# Revit family: OPUS-B
name_source: partatom
category: Mechanical Equipment
revit_build: Autodesk Revit 2015 (Build: 20140606_1530(x64)
units: mm (PartAtom-declared; Revit-internal decimal feet)

## types (6) — shared parameters
Catalogue Pages = http://www.nuaire.info
Depth = 160 mm  [stored 0.524934 ft]
Electrical Phase = 1
Fax Number = +44(0)2920-858-222
Height = 320 mm  [stored 1.04987 ft]
I&M Manual = http://www.nuaire.info
IFCExportAs = IfcFanType
Manufacturer = Nuaire
Manufacturer Name = Nuaire
Maximum Ambient Temperature = 40 °C
OmniClass Number = 23-33 31 19 13
OmniClass Title = Centrifugal Fans
Postcode = CF83 1NA
Revit Family Last Revised = 30/10/18
Spigot Diameter = 125 mm  [stored 0.410105 ft]
Spigot Radius = 63 mm
Telephone Number = +44(0)2920-858-200
URL = http://www.nuaire.co.uk
VAT Registration Number = 877308
Voltage = 230 V
Warranty Period = 3 Years
Weatherproof or Internal Only = Internal
Weight = 6.00 kg
Width = 335 mm  [stored 1.09908 ft]

## per-type parameters (varying)
| type | Apparent Load | Classification.Uniclass.Pr.Description | Classification.Uniclass.Pr.Number | Description | Full Load Current | Model | Nuaire Model Code | Number of Connection Poles | PIR | Starting Current | Unit Description |
| OPUS150-BP | 179 VA | Centrifugal fans | Pr_65_67_29_12 | Surface Mounted Fan Unit with Integral PIR | 1 A | OPUS150-BP | OPUS150-BP | 2 | Yes | 1 A | Surface Mounted Fan Unit with Integral PIR |
| OPUS100-BP | 90 VA | Centrifugal fans | Pr_65_67_29_12 | Surface Mounted Fan Unit with Integral PIR | 0 A | OPUS100-BP | OPUS100-BP | 1 | Yes | 0 A | Surface Mounted Fan Unit with Integral PIR |
| OPUS100-B | 90 VA | Centrifugal fans | Pr_65_67_29_12 | Surface Mounted Fan Unit | 0 A | OPUS100-B | OPUS100-B | 1 | No | 0 A | Surface Mounted Fan Unit |
| OPUS150-B | 179 VA | Centrifugal fans | Pr_65_67_29_12 | Surface Mounted Fan Unit | 1 A | OPUS150-BP | OPUS150-BP | 1 | No | 1 A | Surface Mounted Fan Unit |
| OPUS100-2B | 90 VA | Twin centrifugal fans | Pr_65_67_29_89 | Surface Mounted Twin Fan Unit | 0 A | OPUS100-2B | OPUS100-2B | 1 | No | 0 A | Surface Mounted Twin Fan Unit |
| OPUS100-2BP | 90 VA | Twin centrifugal fans | Pr_65_67_29_89 | Surface Mounted Twin Fan Unit with integral PIR | 0 A | OPUS100-2B | OPUS100-2B | 1 | Yes | 0 A | Surface Mounted Twin Fan Unit with integral PIR |

note: [stored X ft] marks values corroborated as IEEE doubles in the binary element streams (Revit-internal decimal feet)

## geometry (parser evidence)
native form markers: Blend x2, Sweep x10
no freeform markers — native parametric forms only
